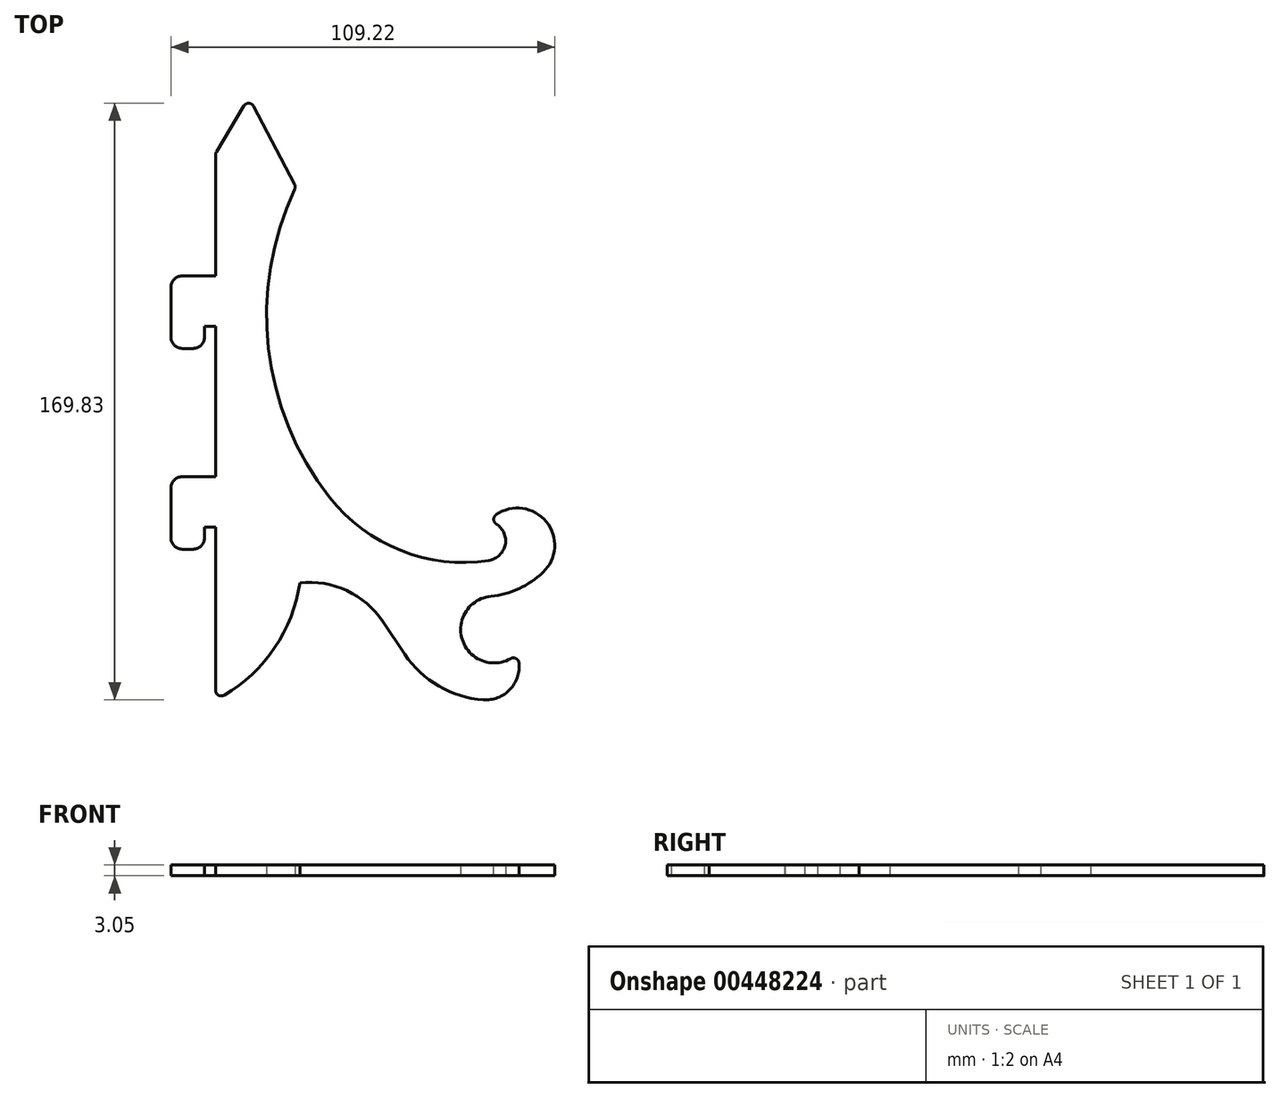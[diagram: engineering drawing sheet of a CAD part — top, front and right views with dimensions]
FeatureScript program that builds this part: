
annotation { "Feature Type Name" : "Feature", "Feature Type Description" : "" }
export const myFeature = defineFeature(function(context is Context, id is Id, definition is map)
    precondition{}
    {
        {
            var Q0;
            Q0=qCreatedBy(makeId("Top.planeOp"),FACE);
            var sketch = newSketch(context, id + "F0", { "sketchPlane" : qUnion([Q0])});
            skLineSegment(sketch, "E0", {"start": v(0, 0) * mm, "end": v(0, 155.58) * mm});
            skLineSegment(sketch, "E1", {"start": v(0, 155.58) * mm, "end": v(9.52, 171.45) * mm});
            skLineSegment(sketch, "E2", {"start": v(9.53, 171.45) * mm, "end": v(22.86, 146.05) * mm});
            skArc(sketch, "E3", {"start": v(0, 0) * mm, "mid": v(16.07, 13.73) * mm, "end": v(23.97, 33.34) * mm});
            skArc(sketch, "E4", {"start": v(47.62, 22.23) * mm, "mid": v(37.34, 31.06) * mm, "end": v(23.97, 33.34) * mm});
            skLineSegment(sketch, "E5", {"start": v(47.62, 22.23) * mm, "end": v(53.82, 13) * mm});
            skArc(sketch, "E6", {"start": v(53.82, 13) * mm, "mid": v(63.51, 3.92) * mm, "end": v(76.2, 0) * mm});
            skArc(sketch, "E7", {"start": v(76.2, 0) * mm, "mid": v(84.56, 3.86) * mm, "end": v(85.73, 13) * mm});
            skArc(sketch, "E8", {"start": v(78.35, 29.47) * mm, "mid": v(70.6, 16.1) * mm, "end": v(85.72, 13) * mm});
            skArc(sketch, "E9", {"start": v(78.35, 29.47) * mm, "mid": v(86.36, 31.63) * mm, "end": v(93.22, 36.28) * mm});
            skArc(sketch, "E10", {"start": v(22.86, 146.05) * mm, "mid": v(15, 100.47) * mm, "end": v(32.42, 57.61) * mm});
            skArc(sketch, "E11", {"start": v(32.42, 57.61) * mm, "mid": v(52.67, 42.5) * mm, "end": v(77.79, 39.69) * mm});
            skArc(sketch, "E12", {"start": v(77.79, 39.69) * mm, "mid": v(82.55, 45.24) * mm, "end": v(77.79, 50.8) * mm});
            skArc(sketch, "E13", {"start": v(93.22, 36.28) * mm, "mid": v(93.18, 51.7) * mm, "end": v(77.79, 50.8) * mm});
            skSolve(sketch);
        }
        {
            var Q0;
            Q0=makeQuery(id+"F0.imprint","IMPRINT",FACE,{"disambiguationData":[TD([[makeQuery(id+"F0.imprint","IMPRINT",EDGE,{"derivedFrom":sQuery(id+"F0.wireOp",EDGE,"E0")}),-1.0]])]});
            extrude(context, id + "F1", {"entities" : qUnion([Q0]), "depth" : 3.05 * mm, "offsetDistance" : 25.4 * mm});
        }
        {
            var Q0;
            Q0=makeQuery(id+"F1.opExtrude","SWEPT_EDGE",EDGE,{"disambiguationData":[OSD([sQuery(id+"F0.wireOp",EDGE,"E0"),sQuery(id+"F0.wireOp",EDGE,"E3")])]});
            fillet(context, id + "F2", {"entities" : qUnion([Q0]), "radius" : 1.59 * mm, "tangentPropagation" : true, "allowEdgeOverflow" : false});
        }
        {
            var Q0;
            Q0=makeQuery(id+"F1.opExtrude","SWEPT_EDGE",EDGE,{"disambiguationData":[OSD([sQuery(id+"F0.wireOp",EDGE,"E7"),sQuery(id+"F0.wireOp",EDGE,"E8")])]});
            var Q1;
            Q1=makeQuery(id+"F1.opExtrude","SWEPT_EDGE",EDGE,{"disambiguationData":[OSD([sQuery(id+"F0.wireOp",EDGE,"E2"),sQuery(id+"F0.wireOp",EDGE,"E10")])]});
            var Q2;
            Q2=makeQuery(id+"F1.opExtrude","SWEPT_EDGE",EDGE,{"disambiguationData":[OSD([sQuery(id+"F0.wireOp",EDGE,"E1"),sQuery(id+"F0.wireOp",EDGE,"E2")])]});
            var Q3;
            Q3=makeQuery(id+"F1.opExtrude","SWEPT_EDGE",EDGE,{"disambiguationData":[OSD([sQuery(id+"F0.wireOp",EDGE,"E0"),sQuery(id+"F0.wireOp",EDGE,"E1")])]});
            var Q4;
            Q4=makeQuery(id+"F1.opExtrude","SWEPT_EDGE",EDGE,{"disambiguationData":[OSD([sQuery(id+"F0.wireOp",EDGE,"E12"),sQuery(id+"F0.wireOp",EDGE,"E13")])]});
            fillet(context, id + "F3", {"entities" : qUnion([Q0, Q1, Q2, Q3, Q4]), "radius" : 1.59 * mm, "tangentPropagation" : true, "allowEdgeOverflow" : false});
        }
        {
            var Q0;
            Q0=makeQuery(id+"F1.opExtrude","SWEPT_BODY",BODY,{"disambiguationData":[OSD([sQuery(id+"F0.wireOp",EDGE,"E0"),sQuery(id+"F0.wireOp",EDGE,"E1"),sQuery(id+"F0.wireOp",EDGE,"E2"),sQuery(id+"F0.wireOp",EDGE,"E3"),sQuery(id+"F0.wireOp",EDGE,"E4"),sQuery(id+"F0.wireOp",EDGE,"E5"),sQuery(id+"F0.wireOp",EDGE,"E6"),sQuery(id+"F0.wireOp",EDGE,"E7"),sQuery(id+"F0.wireOp",EDGE,"E8"),sQuery(id+"F0.wireOp",EDGE,"E9"),sQuery(id+"F0.wireOp",EDGE,"E10"),sQuery(id+"F0.wireOp",EDGE,"E11"),sQuery(id+"F0.wireOp",EDGE,"E12"),sQuery(id+"F0.wireOp",EDGE,"E13")])]});
            transform(context, id + "F4", {"entities" : qUnion([Q0]), "transformType" : TransformType.TRANSLATION_3D, "dx" : 0 * mm, "dy" : 0 * mm, "dz" : 0 * mm, "makeCopy" : true});
        }
        {
            var Q0;
            Q0=makeQuery(id+"F1.opExtrude","CAP_FACE",FACE,{"disambiguationData":[OSD([sQuery(id+"F0.wireOp",EDGE,"E0"),sQuery(id+"F0.wireOp",EDGE,"E1"),sQuery(id+"F0.wireOp",EDGE,"E2"),sQuery(id+"F0.wireOp",EDGE,"E3"),sQuery(id+"F0.wireOp",EDGE,"E4"),sQuery(id+"F0.wireOp",EDGE,"E5"),sQuery(id+"F0.wireOp",EDGE,"E6"),sQuery(id+"F0.wireOp",EDGE,"E7"),sQuery(id+"F0.wireOp",EDGE,"E8"),sQuery(id+"F0.wireOp",EDGE,"E9"),sQuery(id+"F0.wireOp",EDGE,"E10"),sQuery(id+"F0.wireOp",EDGE,"E11"),sQuery(id+"F0.wireOp",EDGE,"E12"),sQuery(id+"F0.wireOp",EDGE,"E13")])],"isStart":false});
            var sketch = newSketch(context, id + "F5", { "sketchPlane" : qUnion([Q0])});
            skLineSegment(sketch, "E14", {"start": v(0, 120.65) * mm, "end": v(-12.7, 120.65) * mm});
            skLineSegment(sketch, "E15", {"start": v(-12.7, 120.65) * mm, "end": v(-12.7, 100.01) * mm});
            skLineSegment(sketch, "E16", {"start": v(-12.7, 100.01) * mm, "end": v(-3.18, 100.01) * mm});
            skLineSegment(sketch, "E17", {"start": v(-3.18, 100.01) * mm, "end": v(-3.18, 106.36) * mm});
            skLineSegment(sketch, "E18", {"start": v(-3.18, 106.36) * mm, "end": v(0, 106.36) * mm});
            skLineSegment(sketch, "E19", {"start": v(0, 120.65) * mm, "end": v(0, 106.36) * mm});
            skLineSegment(sketch, "E20", {"start": v(0, 63.5) * mm, "end": v(-12.7, 63.5) * mm});
            skLineSegment(sketch, "E21", {"start": v(-12.7, 63.5) * mm, "end": v(-12.7, 42.86) * mm});
            skLineSegment(sketch, "E22", {"start": v(-12.7, 42.86) * mm, "end": v(-3.18, 42.86) * mm});
            skLineSegment(sketch, "E23", {"start": v(-3.18, 42.86) * mm, "end": v(-3.18, 49.21) * mm});
            skLineSegment(sketch, "E24", {"start": v(-3.18, 49.21) * mm, "end": v(0, 49.21) * mm});
            skLineSegment(sketch, "E25", {"start": v(0, 49.21) * mm, "end": v(0, 63.5) * mm});
            skSolve(sketch);
        }
        {
            var Q0;
            Q0=makeQuery(id+"F5.imprint","IMPRINT",FACE,{"disambiguationData":[TD([[makeQuery(id+"F5.imprint","IMPRINT",EDGE,{"derivedFrom":sQuery(id+"F5.wireOp",EDGE,"E20")}),1.0]])]});
            var Q1;
            Q1=makeQuery(id+"F5.imprint","IMPRINT",FACE,{"disambiguationData":[TD([[makeQuery(id+"F5.imprint","IMPRINT",EDGE,{"derivedFrom":sQuery(id+"F5.wireOp",EDGE,"E14")}),1.0]])]});
            extrude(context, id + "F6", {"entities" : qUnion([Q0, Q1]), "operationType" : NewBodyOperationType.ADD, "oppositeDirection" : true, "depth" : 3.05 * mm, "offsetDistance" : 25.4 * mm});
        }
        {
            var Q0;
            Q0=makeQuery(id+"F6.opExtrude","SWEPT_EDGE",EDGE,{"disambiguationData":[OSD([sQuery(id+"F5.wireOp",EDGE,"E14"),sQuery(id+"F5.wireOp",EDGE,"E15")])]});
            var Q1;
            Q1=makeQuery(id+"F6.opExtrude","SWEPT_EDGE",EDGE,{"disambiguationData":[OSD([sQuery(id+"F5.wireOp",EDGE,"E15"),sQuery(id+"F5.wireOp",EDGE,"E16")])]});
            var Q2;
            Q2=makeQuery(id+"F6.opExtrude","SWEPT_EDGE",EDGE,{"disambiguationData":[OSD([sQuery(id+"F5.wireOp",EDGE,"E20"),sQuery(id+"F5.wireOp",EDGE,"E21")])]});
            var Q3;
            Q3=makeQuery(id+"F6.opExtrude","SWEPT_EDGE",EDGE,{"disambiguationData":[OSD([sQuery(id+"F5.wireOp",EDGE,"E21"),sQuery(id+"F5.wireOp",EDGE,"E22")])]});
            var Q4;
            Q4=makeQuery(id+"F6.opExtrude","SWEPT_EDGE",EDGE,{"disambiguationData":[OSD([sQuery(id+"F5.wireOp",EDGE,"E16"),sQuery(id+"F5.wireOp",EDGE,"E17")])]});
            var Q5;
            Q5=makeQuery(id+"F6.opExtrude","SWEPT_EDGE",EDGE,{"disambiguationData":[OSD([sQuery(id+"F5.wireOp",EDGE,"E22"),sQuery(id+"F5.wireOp",EDGE,"E23")])]});
            fillet(context, id + "F7", {"entities" : qUnion([Q0, Q1, Q2, Q3, Q4, Q5]), "radius" : 3.17 * mm, "tangentPropagation" : true, "allowEdgeOverflow" : false});
        }
    });
